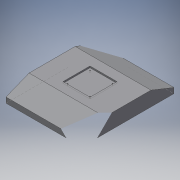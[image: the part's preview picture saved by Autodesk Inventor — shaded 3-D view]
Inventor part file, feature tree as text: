
AUTODESK INVENTOR PART (.ipt)
format: ipt  version: 2016 (Build 200138000, 138)  size: 126,976 bytes
history: native  units: in
note: dims shown in document units (in); Inventor stores cm internally (conversion verified against a paired STEP export)
features: extrude x4, sketch x4
ambient origin geometry x8: Origin, YZ Plane, XZ Plane, XY Plane, X Axis, Y Axis, Z Axis, Center Point
bodies: Solid1 (feature_tree)
feature tree (8):
  extrude  "Extrusion1"  Depth=13.3in
  extrude  "Extrusion2"  Depth=2.56in
  extrude  "Extrusion3"  Depth=0.94in
  extrude  "Extrusion4"  Depth=4.75in
  sketch  "Sketch1"  dims[d0=16.2in d1=13.3in]
  sketch  "Sketch2"  dims[d2=2.56in d3=0.0in d4=8.1in]
  sketch  "Sketch3"  dims[d5=0.94in d6=0.94in]
  sketch  "Sketch4"  dims[d7=15.2475in d8=0.0in d9=4.75in d10=4.75in d11=0.2812in d12=0.0in d13=0.125in d14=0.125in d15=0.125in d16=0.125in d17=3.937in d18=3.937in d19=3.937in d20=0.3in d21=0.0in]
